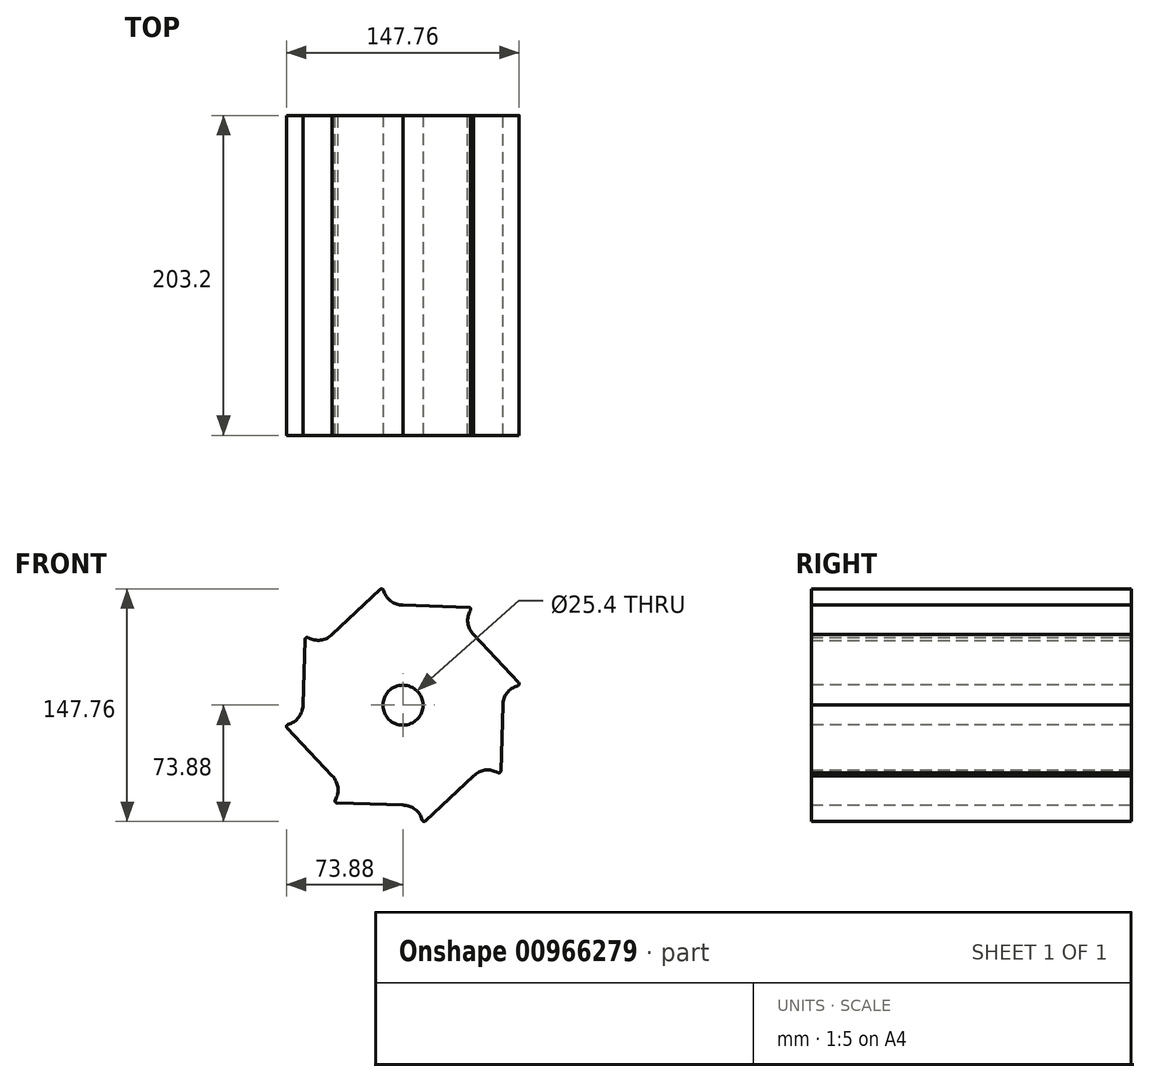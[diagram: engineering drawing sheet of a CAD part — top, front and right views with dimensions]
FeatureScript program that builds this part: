
annotation { "Feature Type Name" : "Feature", "Feature Type Description" : "" }
export const myFeature = defineFeature(function(context is Context, id is Id, definition is map)
    precondition{}
    {
        {
            var Q0;
            Q0=qCreatedBy(makeId("Front.planeOp"),FACE);
            var sketch = newSketch(context, id + "F0", { "sketchPlane" : qUnion([Q0])});
            skCircle(sketch, "E0", {"center": v(0, 0) * mm, "radius": 76.2 * mm});
            skLineSegment(sketch, "E1.bottom", {"start": v(152.4, -101.6) * mm, "end": v(-152.4, -101.6) * mm});
            skLineSegment(sketch, "E1.top", {"start": v(152.4, -254) * mm, "end": v(-152.4, -254) * mm});
            skLineSegment(sketch, "E1.left", {"start": v(152.4, -101.6) * mm, "end": v(152.4, -254) * mm});
            skLineSegment(sketch, "E1.right", {"start": v(-152.4, -101.6) * mm, "end": v(-152.4, -254) * mm});
            skPoint(sketch, "E1.middle", {"position": v(0, -177.8) * mm});
            skLineSegment(sketch, "E2", {"start": v(152.4, -101.6) * mm, "end": v(152.4, -55.75) * mm});
            skLineSegment(sketch, "E3", {"start": v(152.4, -55.75) * mm, "end": v(133.68, -55.75) * mm});
            skLineSegment(sketch, "E4", {"start": v(133.68, -55.75) * mm, "end": v(133.68, -101.6) * mm});
            skLineSegment(sketch, "E5", {"start": v(-152.4, -101.6) * mm, "end": v(133.68, -55.75) * mm});
            skLineSegment(sketch, "E6.bottom", {"start": v(76.2, 76.2) * mm, "end": v(-76.2, 76.2) * mm});
            skLineSegment(sketch, "E6.top", {"start": v(76.2, -76.2) * mm, "end": v(-76.2, -76.2) * mm});
            skLineSegment(sketch, "E6.left", {"start": v(76.2, 76.2) * mm, "end": v(76.2, -76.2) * mm});
            skLineSegment(sketch, "E6.right", {"start": v(-76.2, 76.2) * mm, "end": v(-76.2, -76.2) * mm});
            skLineSegment(sketch, "E7", {"start": v(76.2, -76.2) * mm, "end": v(-76.2, 76.2) * mm});
            skLineSegment(sketch, "E8", {"start": v(76.2, 76.2) * mm, "end": v(-76.2, -76.2) * mm});
            skCircle(sketch, "E9", {"center": v(53.88, -53.88) * mm, "radius": 12.7 * mm});
            skCircle(sketch, "E10", {"center": v(53.88, 53.88) * mm, "radius": 12.7 * mm});
            skCircle(sketch, "E11", {"center": v(-53.88, 53.88) * mm, "radius": 12.7 * mm});
            skCircle(sketch, "E12", {"center": v(-53.88, -53.88) * mm, "radius": 12.7 * mm});
            skCircle(sketch, "E13", {"center": v(76.2, 0) * mm, "radius": 12.7 * mm});
            skCircle(sketch, "E14", {"center": v(0, 76.2) * mm, "radius": 12.7 * mm});
            skCircle(sketch, "E15", {"center": v(-76.2, 0) * mm, "radius": 12.7 * mm});
            skCircle(sketch, "E16", {"center": v(0, -76.2) * mm, "radius": 12.7 * mm});
            skLineSegment(sketch, "E17", {"start": v(63.5, 0) * mm, "end": v(62.08, -44.18) * mm});
            skLineSegment(sketch, "E18", {"start": v(44.9, -44.9) * mm, "end": v(12.66, -75.14) * mm});
            skLineSegment(sketch, "E19", {"start": v(0, -63.5) * mm, "end": v(-44.18, -62.08) * mm});
            skLineSegment(sketch, "E20", {"start": v(-44.9, -44.9) * mm, "end": v(-75.14, -12.66) * mm});
            skLineSegment(sketch, "E21", {"start": v(-63.5, 0) * mm, "end": v(-62.08, 44.18) * mm});
            skLineSegment(sketch, "E22", {"start": v(-44.9, 44.9) * mm, "end": v(-12.66, 75.14) * mm});
            skLineSegment(sketch, "E23", {"start": v(0, 63.5) * mm, "end": v(44.18, 62.08) * mm});
            skLineSegment(sketch, "E24", {"start": v(44.9, 44.9) * mm, "end": v(75.14, 12.66) * mm});
            skSolve(sketch);
        }
        {
            var Q0;
            {var subQ0=sQuery(id+"F0.wireOp",EDGE,"E18");Q0=makeQuery(id+"F0.imprint","IMPRINT",FACE,{"disambiguationData":[TD([[makeQuery(id+"F0.imprint","IMPRINT",EDGE,{"derivedFrom":subQ0}),-1.0]])]});}
            var Q1;
            {var subQ0=sQuery(id+"F0.wireOp",EDGE,"E17");Q1=makeQuery(id+"F0.imprint","IMPRINT",FACE,{"disambiguationData":[TD([[makeQuery(id+"F0.imprint","IMPRINT",EDGE,{"derivedFrom":subQ0}),-1.0]])]});}
            var Q2;
            {var subQ7=sQuery(id+"F0.wireOp",EDGE,"E22");Q2=makeQuery(id+"F0.imprint","IMPRINT",FACE,{"disambiguationData":[TD([[makeQuery(id+"F0.imprint","IMPRINT",EDGE,{"derivedFrom":subQ7}),-1.0]])]});}
            var Q3;
            {var subQ0=sQuery(id+"F0.wireOp",EDGE,"E20");Q3=makeQuery(id+"F0.imprint","IMPRINT",FACE,{"disambiguationData":[TD([[makeQuery(id+"F0.imprint","IMPRINT",EDGE,{"derivedFrom":subQ0}),-1.0]])]});}
            extrude(context, id + "F1", {"entities" : qUnion([Q0, Q1, Q2, Q3]), "depth" : 203.2 * mm, "offsetDistance" : 25.4 * mm});
        }
        {
            var Q0;
            Q0=makeQuery(id+"F1.opExtrude","CAP_FACE",FACE,{"disambiguationData":[OSD([sQuery(id+"F0.wireOp",EDGE,"E9"),sQuery(id+"F0.wireOp",EDGE,"E10"),sQuery(id+"F0.wireOp",EDGE,"E11"),sQuery(id+"F0.wireOp",EDGE,"E12"),sQuery(id+"F0.wireOp",EDGE,"E13"),sQuery(id+"F0.wireOp",EDGE,"E14"),sQuery(id+"F0.wireOp",EDGE,"E15"),sQuery(id+"F0.wireOp",EDGE,"E16"),sQuery(id+"F0.wireOp",EDGE,"E17"),sQuery(id+"F0.wireOp",EDGE,"E18"),sQuery(id+"F0.wireOp",EDGE,"E19"),sQuery(id+"F0.wireOp",EDGE,"E20"),sQuery(id+"F0.wireOp",EDGE,"E21"),sQuery(id+"F0.wireOp",EDGE,"E22"),sQuery(id+"F0.wireOp",EDGE,"E23"),sQuery(id+"F0.wireOp",EDGE,"E24")])],"isStart":false});
            var sketch = newSketch(context, id + "F2", { "sketchPlane" : qUnion([Q0])});
            skCircle(sketch, "E25", {"center": v(0, 0) * mm, "radius": 12.7 * mm});
            skSolve(sketch);
        }
        {
            var Q0;
            Q0 = qSketchRegion(id + "F2", true);
            extrude(context, id + "F3", {"entities" : qUnion([Q0]), "operationType" : NewBodyOperationType.REMOVE, "endBound" : BoundingType.THROUGH_ALL, "oppositeDirection" : true, "depth" : 25.4 * mm, "offsetDistance" : 25.4 * mm});
        }
        {
            var Q0;
            Q0=makeQuery(id+"F1.opExtrude","SWEPT_EDGE",EDGE,{"disambiguationData":[OSD([sQuery(id+"F0.wireOp",EDGE,"E0"),sQuery(id+"F0.wireOp",EDGE,"E14"),sQuery(id+"F0.wireOp",EDGE,"E22")])]});
            var Q1;
            Q1=makeQuery(id+"F1.opExtrude","SWEPT_EDGE",EDGE,{"disambiguationData":[OSD([sQuery(id+"F0.wireOp",EDGE,"E0"),sQuery(id+"F0.wireOp",EDGE,"E10"),sQuery(id+"F0.wireOp",EDGE,"E23")])]});
            var Q2;
            Q2=makeQuery(id+"F1.opExtrude","SWEPT_EDGE",EDGE,{"disambiguationData":[OSD([sQuery(id+"F0.wireOp",EDGE,"E0"),sQuery(id+"F0.wireOp",EDGE,"E11"),sQuery(id+"F0.wireOp",EDGE,"E21")])]});
            var Q3;
            Q3=makeQuery(id+"F1.opExtrude","SWEPT_EDGE",EDGE,{"disambiguationData":[OSD([sQuery(id+"F0.wireOp",EDGE,"E0"),sQuery(id+"F0.wireOp",EDGE,"E15"),sQuery(id+"F0.wireOp",EDGE,"E20")])]});
            var Q4;
            Q4=makeQuery(id+"F1.opExtrude","SWEPT_EDGE",EDGE,{"disambiguationData":[OSD([sQuery(id+"F0.wireOp",EDGE,"E0"),sQuery(id+"F0.wireOp",EDGE,"E12"),sQuery(id+"F0.wireOp",EDGE,"E19")])]});
            var Q5;
            Q5=makeQuery(id+"F1.opExtrude","SWEPT_EDGE",EDGE,{"disambiguationData":[OSD([sQuery(id+"F0.wireOp",EDGE,"E0"),sQuery(id+"F0.wireOp",EDGE,"E16"),sQuery(id+"F0.wireOp",EDGE,"E18")])]});
            var Q6;
            Q6=makeQuery(id+"F1.opExtrude","SWEPT_EDGE",EDGE,{"disambiguationData":[OSD([sQuery(id+"F0.wireOp",EDGE,"E0"),sQuery(id+"F0.wireOp",EDGE,"E9"),sQuery(id+"F0.wireOp",EDGE,"E17")])]});
            var Q7;
            Q7=makeQuery(id+"F1.opExtrude","SWEPT_EDGE",EDGE,{"disambiguationData":[OSD([sQuery(id+"F0.wireOp",EDGE,"E0"),sQuery(id+"F0.wireOp",EDGE,"E13"),sQuery(id+"F0.wireOp",EDGE,"E24")])]});
            fillet(context, id + "F4", {"entities" : qUnion([Q0, Q1, Q2, Q3, Q4, Q5, Q6, Q7]), "radius" : 1.27 * mm, "tangentPropagation" : true, "allowEdgeOverflow" : false});
        }
    });
